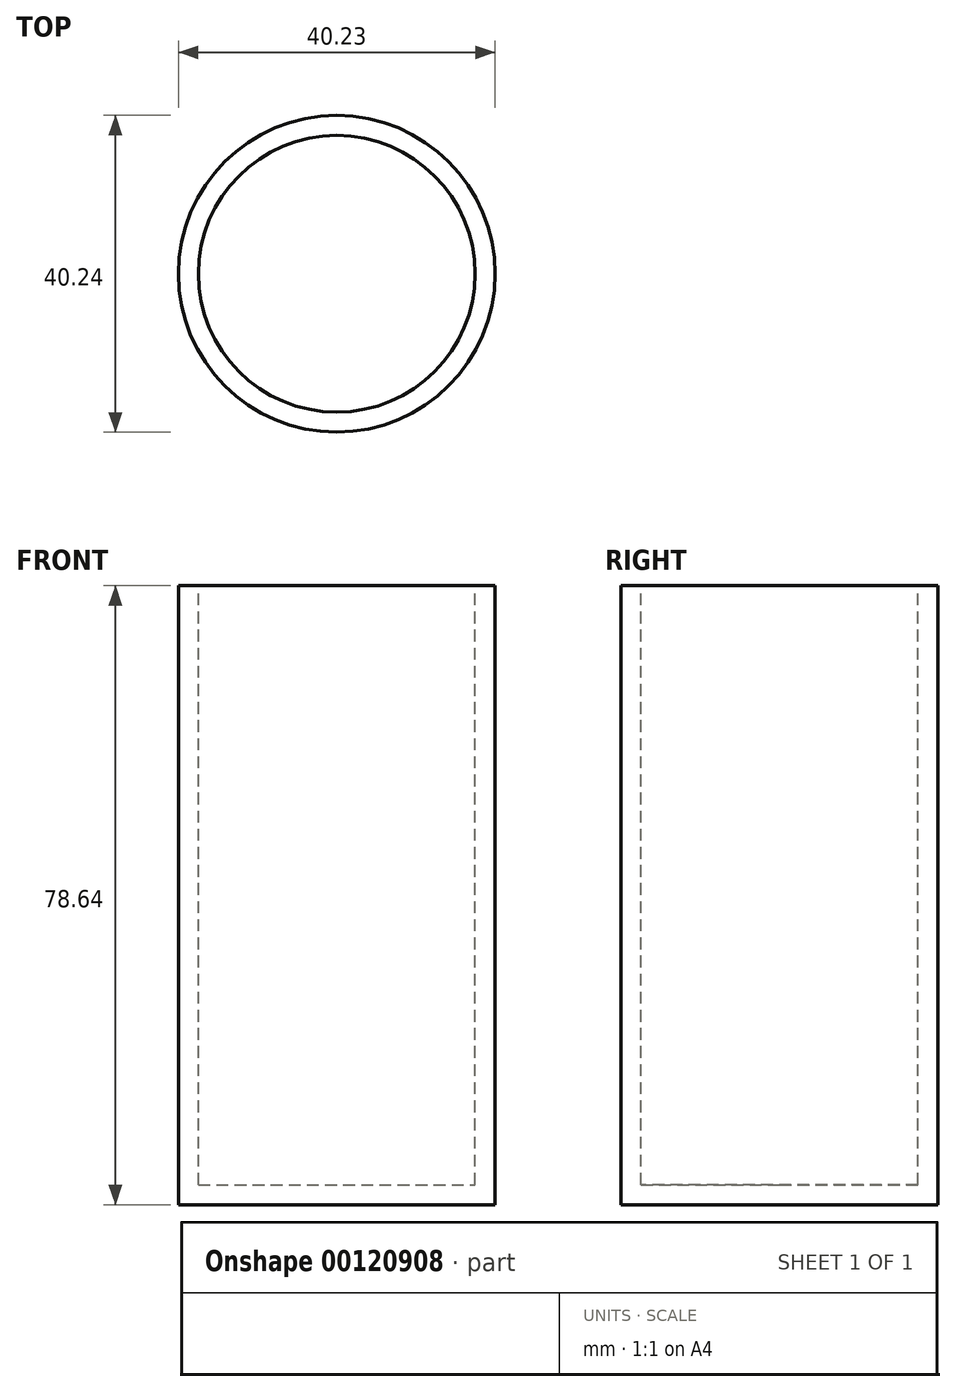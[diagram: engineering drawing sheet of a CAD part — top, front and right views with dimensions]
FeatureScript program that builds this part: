
annotation { "Feature Type Name" : "Feature", "Feature Type Description" : "" }
export const myFeature = defineFeature(function(context is Context, id is Id, definition is map)
    precondition{}
    {
        {
            var Q0;
            Q0=qCreatedBy(makeId("Front.planeOp"),FACE);
            var sketch = newSketch(context, id + "F0", { "sketchPlane" : qUnion([Q0])});
            skLineSegment(sketch, "E0.bottom", {"start": v(-33.22, 13.26) * mm, "end": v(-13.1, 13.26) * mm});
            skLineSegment(sketch, "E0.top", {"start": v(-33.22, -65.38) * mm, "end": v(-13.1, -65.38) * mm});
            skLineSegment(sketch, "E0.left", {"start": v(-33.22, 13.26) * mm, "end": v(-33.22, -65.38) * mm});
            skLineSegment(sketch, "E0.right", {"start": v(-13.1, 13.26) * mm, "end": v(-13.1, -65.38) * mm});
            skSolve(sketch);
        }
        {
            var Q0;
            Q0 = qSketchRegion(id + "F0", true);
            var Q1;
            Q1=sQuery(id+"F0.wireOp",EDGE,"E0.right");
            revolve(context, id + "F1", {"entities" : qUnion([Q0]), "axis" : qUnion([Q1]), "revolveType" : RevolveType.FULL});
        }
        {
            var Q0;
            Q0=makeQuery(id+"F1.opRevolve","SWEPT_FACE",FACE,{"disambiguationData":[OSD([sQuery(id+"F0.wireOp",EDGE,"E0.bottom")])]});
            shell(context, id + "F2", {"entities" : qUnion([Q0]), "thickness" : 2.54 * mm});
        }
    });
